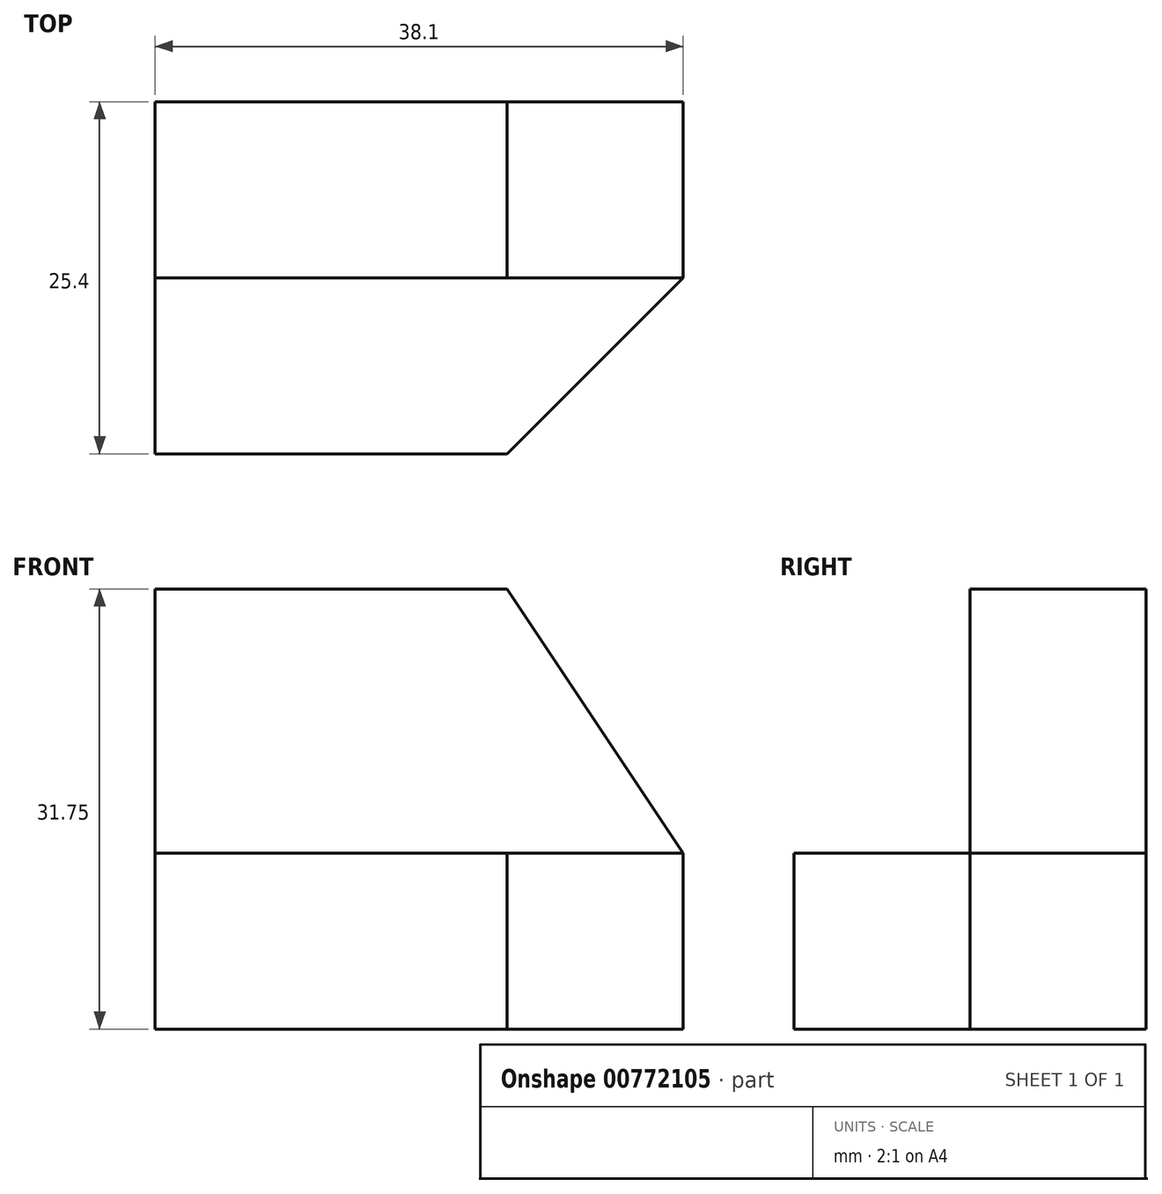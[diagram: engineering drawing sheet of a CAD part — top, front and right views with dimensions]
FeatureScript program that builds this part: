
annotation { "Feature Type Name" : "Feature", "Feature Type Description" : "" }
export const myFeature = defineFeature(function(context is Context, id is Id, definition is map)
    precondition{}
    {
        {
            var Q0;
            Q0=qCreatedBy(makeId("Right.planeOp"),FACE);
            var sketch = newSketch(context, id + "F0", { "sketchPlane" : qUnion([Q0])});
            skLineSegment(sketch, "E0", {"start": v(0, 0) * mm, "end": v(25.4, 0) * mm});
            skLineSegment(sketch, "E1", {"start": v(25.4, 0) * mm, "end": v(25.4, 31.75) * mm});
            skLineSegment(sketch, "E2", {"start": v(25.4, 31.75) * mm, "end": v(12.7, 31.75) * mm});
            skLineSegment(sketch, "E3", {"start": v(12.7, 31.75) * mm, "end": v(12.7, 12.7) * mm});
            skLineSegment(sketch, "E4", {"start": v(12.7, 12.7) * mm, "end": v(0, 12.7) * mm});
            skLineSegment(sketch, "E5", {"start": v(0, 12.7) * mm, "end": v(0, 0) * mm});
            skSolve(sketch);
        }
        {
            var Q0;
            Q0=makeQuery(id+"F0.imprint","IMPRINT",FACE,{"disambiguationData":[TD([[makeQuery(id+"F0.imprint","IMPRINT",EDGE,{"derivedFrom":sQuery(id+"F0.wireOp",EDGE,"E0")}),1.0]])]});
            extrude(context, id + "F1", {"entities" : qUnion([Q0]), "depth" : 38.1 * mm, "offsetDistance" : 25.4 * mm});
        }
        {
            var Q0;
            Q0=makeQuery(id+"F1.opExtrude","SWEPT_FACE",FACE,{"disambiguationData":[OSD([sQuery(id+"F0.wireOp",EDGE,"E4")])]});
            var sketch = newSketch(context, id + "F2", { "sketchPlane" : qUnion([Q0])});
            skLineSegment(sketch, "E6", {"start": v(38.1, 0) * mm, "end": v(25.4, 0) * mm});
            skLineSegment(sketch, "E7", {"start": v(25.4, 0) * mm, "end": v(38.1, 12.7) * mm});
            skSolve(sketch);
        }
        {
            var Q0;
            Q0 = qSketchRegion(id + "F2", true);
            var Q1;
            Q1=makeQuery(id+"F2.imprint","IMPRINT",FACE,{"disambiguationData":[TD([[makeQuery(id+"F2.imprint","IMPRINT",EDGE,{"derivedFrom":sQuery(id+"F2.wireOp",EDGE,"E6")}),-1.0]])]});
            extrude(context, id + "F3", {"entities" : qUnion([Q0, Q1]), "operationType" : NewBodyOperationType.REMOVE, "oppositeDirection" : true, "depth" : 25.4 * mm, "offsetDistance" : 25.4 * mm});
        }
        {
            var Q0;
            Q0=makeQuery(id+"F1.opExtrude","SWEPT_FACE",FACE,{"disambiguationData":[OSD([sQuery(id+"F0.wireOp",EDGE,"E3")])]});
            var sketch = newSketch(context, id + "F4", { "sketchPlane" : qUnion([Q0])});
            skLineSegment(sketch, "E8", {"start": v(0, 31.75) * mm, "end": v(25.4, 31.75) * mm});
            skLineSegment(sketch, "E9", {"start": v(25.4, 31.75) * mm, "end": v(38.1, 12.7) * mm});
            skSolve(sketch);
        }
        {
            var Q0;
            Q0 = qSketchRegion(id + "F4", true);
            var Q1;
            {var subQ0=sQuery(id+"F4.wireOp",EDGE,"E9");Q1=makeQuery(id+"F4.imprint","IMPRINT",FACE,{"disambiguationData":[TD([[makeQuery(id+"F4.imprint","IMPRINT",EDGE,{"derivedFrom":subQ0}),1.0]])]});}
            extrude(context, id + "F5", {"entities" : qUnion([Q0, Q1]), "operationType" : NewBodyOperationType.REMOVE, "oppositeDirection" : true, "depth" : 25.4 * mm, "offsetDistance" : 25.4 * mm});
        }
    });
